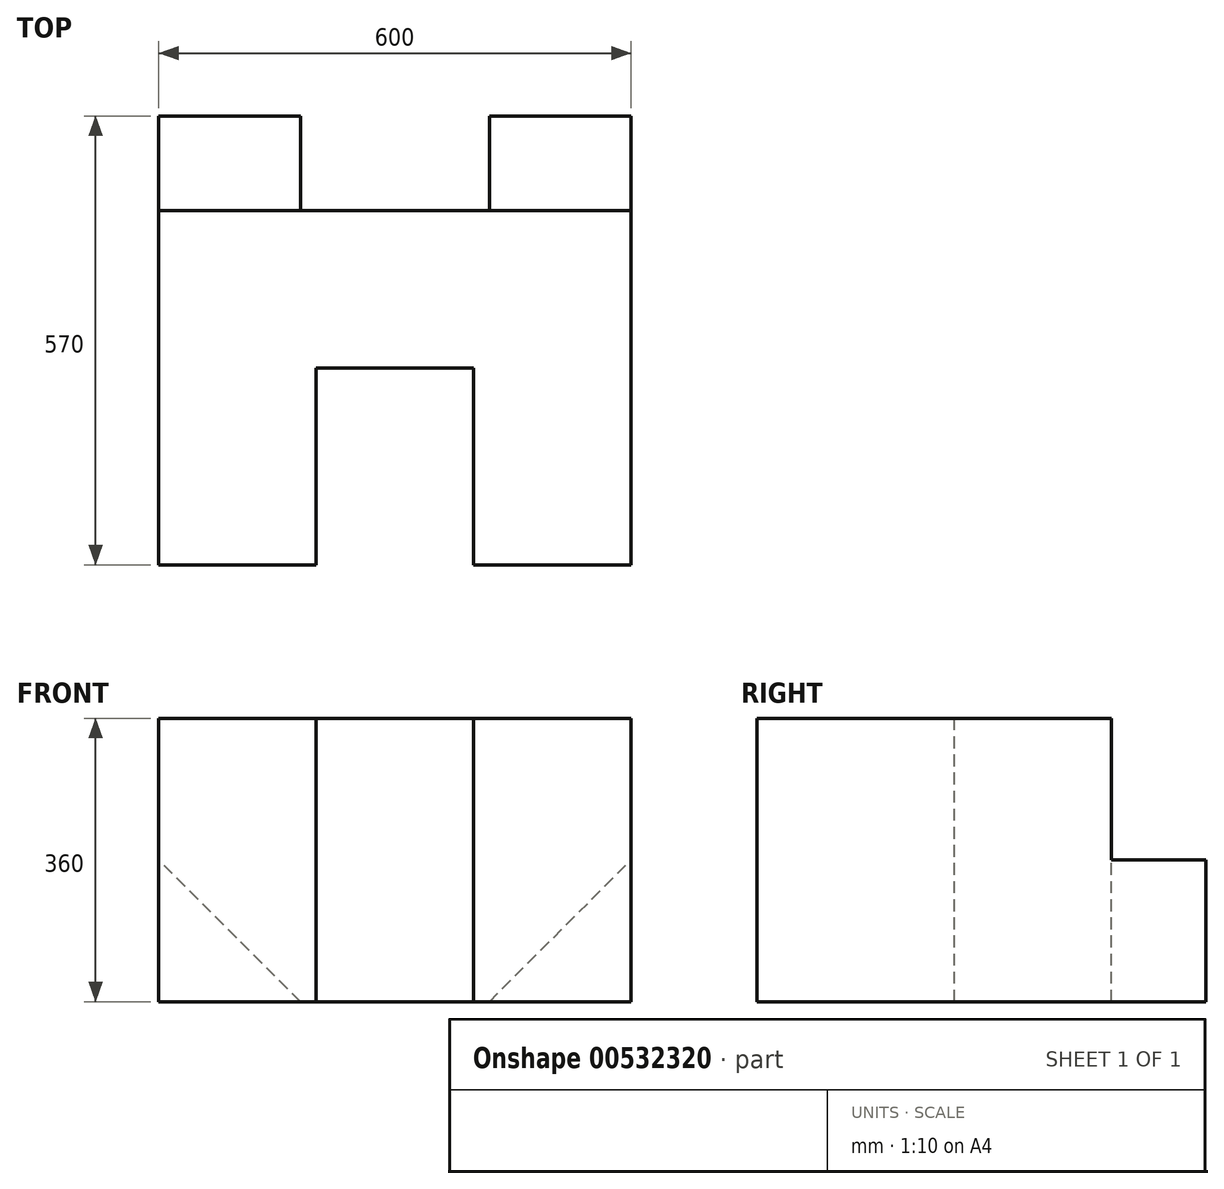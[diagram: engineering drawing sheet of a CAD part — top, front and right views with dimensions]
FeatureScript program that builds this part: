
annotation { "Feature Type Name" : "Feature", "Feature Type Description" : "" }
export const myFeature = defineFeature(function(context is Context, id is Id, definition is map)
    precondition{}
    {
        {
            var Q0;
            Q0=qCreatedBy(makeId("Top.planeOp"),FACE);
            var sketch = newSketch(context, id + "F0", { "sketchPlane" : qUnion([Q0])});
            skLineSegment(sketch, "E0.bottom", {"start": v(300, -225) * mm, "end": v(100, -225) * mm});
            skLineSegment(sketch, "E0.top", {"start": v(300, 225) * mm, "end": v(-300, 225) * mm});
            skLineSegment(sketch, "E0.left", {"start": v(300, -225) * mm, "end": v(300, 225) * mm});
            skLineSegment(sketch, "E0.right", {"start": v(-300, -225) * mm, "end": v(-300, 225) * mm});
            skPoint(sketch, "E0.middle", {"position": v(0, 0) * mm});
            skLineSegment(sketch, "E1.bottom", {"start": v(-100, 25) * mm, "end": v(100, 25) * mm});
            skLineSegment(sketch, "E1.left", {"start": v(-100, 25) * mm, "end": v(-100, -225) * mm});
            skLineSegment(sketch, "E1.right", {"start": v(100, 25) * mm, "end": v(100, -225) * mm});
            skPoint(sketch, "E1.middle", {"position": v(0, -225) * mm});
            skPoint(sketch, "E1.top.start.orphan", {"position": v(-100, -475) * mm});
            skPoint(sketch, "E2.orphan", {"position": v(100, -475) * mm});
            skLineSegment(sketch, "E3.trimOffspring", {"start": v(-100, -225) * mm, "end": v(-300, -225) * mm});
            skSolve(sketch);
        }
        {
            var Q0;
            Q0 = qSketchRegion(id + "F0", true);
            extrude(context, id + "F1", {"entities" : qUnion([Q0]), "depth" : 360 * mm, "offsetDistance" : 25.4 * mm});
        }
        {
            var Q0;
            Q0=makeQuery(id+"F1.opExtrude","SWEPT_FACE",FACE,{"disambiguationData":[OSD([sQuery(id+"F0.wireOp",EDGE,"E0.top")])]});
            var sketch = newSketch(context, id + "F2", { "sketchPlane" : qUnion([Q0])});
            skLineSegment(sketch, "E4", {"start": v(120, 0) * mm, "end": v(300, 180) * mm});
            skLineSegment(sketch, "E5", {"start": v(-120, 0) * mm, "end": v(-300, 180) * mm});
            skSolve(sketch);
        }
        {
            var Q0;
            Q0 = qSketchRegion(id + "F2", true);
            var Q1;
            {var subQ0=sQuery(id+"F2.wireOp",EDGE,"E4");Q1=makeQuery(id+"F2.imprint","IMPRINT",FACE,{"disambiguationData":[TD([[makeQuery(id+"F2.imprint","IMPRINT",EDGE,{"derivedFrom":subQ0}),-1.0]])]});}
            var Q2;
            {var subQ0=sQuery(id+"F2.wireOp",EDGE,"E5");Q2=makeQuery(id+"F2.imprint","IMPRINT",FACE,{"disambiguationData":[TD([[makeQuery(id+"F2.imprint","IMPRINT",EDGE,{"derivedFrom":subQ0}),1.0]])]});}
            extrude(context, id + "F3", {"entities" : qUnion([Q0, Q1, Q2]), "operationType" : NewBodyOperationType.ADD, "depth" : 120 * mm, "offsetDistance" : 25.4 * mm});
        }
    });
